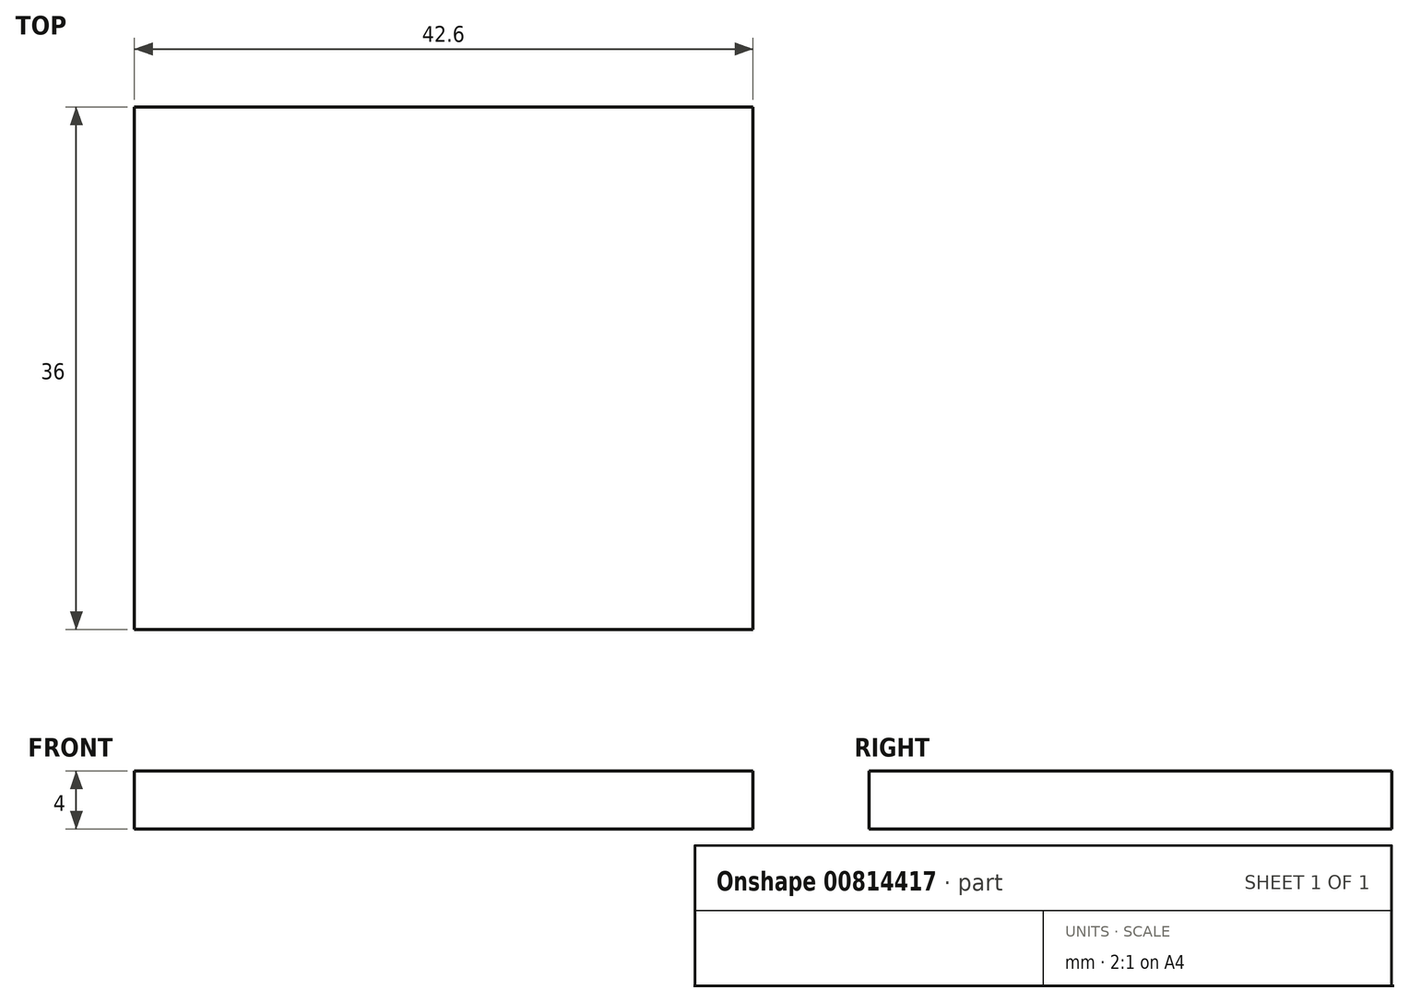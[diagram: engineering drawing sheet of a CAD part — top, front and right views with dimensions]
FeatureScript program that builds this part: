
annotation { "Feature Type Name" : "Feature", "Feature Type Description" : "" }
export const myFeature = defineFeature(function(context is Context, id is Id, definition is map)
    precondition{}
    {
        {
            var Q0;
            Q0=qCreatedBy(makeId("Top.planeOp"),FACE);
            var sketch = newSketch(context, id + "F0", { "sketchPlane" : qUnion([Q0])});
            skLineSegment(sketch, "E0.bottom", {"start": v(0, 0) * mm, "end": v(42.6, 0) * mm});
            skLineSegment(sketch, "E0.top", {"start": v(0, 36) * mm, "end": v(42.6, 36) * mm});
            skLineSegment(sketch, "E0.left", {"start": v(0, 0) * mm, "end": v(0, 36) * mm});
            skLineSegment(sketch, "E0.right", {"start": v(42.6, 0) * mm, "end": v(42.6, 36) * mm});
            skSolve(sketch);
        }
        {
            var Q0;
            Q0=makeQuery(id+"F0.imprint","IMPRINT",FACE,{"disambiguationData":[TD([[makeQuery(id+"F0.imprint","IMPRINT",EDGE,{"derivedFrom":sQuery(id+"F0.wireOp",EDGE,"E0.bottom")}),1.0]])]});
            extrude(context, id + "F1", {"entities" : qUnion([Q0]), "depth" : 4 * mm, "offsetDistance" : 25.4 * mm});
        }
    });
